# Revit family: GMV-ND22-100TC-T
name_source: partatom
category: 机械设备
revit_build: Autodesk Revit 2014 (Build: 20130308_1515(x64)
units: mm (PartAtom-declared; Revit-internal decimal feet)

## types (11) — shared parameters
Drainage Pipe = 25  [stored 0.082021 ft]
Main Body Height = 280  [stored 0.918635 ft]
Main Body Width = 840  [stored 2.75591 ft]
Main body Depth = 840  [stored 2.75591 ft]
Panel Depth = 950
Panel Height = 65
Panel Width = 950
Power supply = 220-240V 1 phase ~50Hz/208-230V 1 phase ~60Hz
主体 = 锌板
主体宽 = 840  [stored 2.75591 ft]
主体深 = 840  [stored 2.75591 ft]
主体高 = 280  [stored 0.918635 ft]
出风口上边到中心线距离 = 380
出风口下边到中心线距离 = 330
出风口右边到中心线距离 = 200  [stored 0.656168 ft]
出风口宽度 = 50  [stored 0.164042 ft]
出风口左边到中心线距离 = 200  [stored 0.656168 ft]
出风口长度 = 400  [stored 1.31234 ft]
吊装孔直径 = 21.71
吊装孔高 = 80
吊装螺杆间距 = 300
回风口边距中心线距离 = 250
回风口长度和宽度 = 500
气管距中心线距离 = 252
气管距面板上边高度 = 89
液管距中心线距离 = 314
液管距面板上边高度 = 115
面板 = ABS

## per-type parameters (varying)
| type | Gas pipe | Liquid pipe | Net weight Main body/Panel(kg) | Sound Pressure Level (H/M/L)(dB) |
| GMV-ND28T/C-T | 9.52 | 6.35  [stored 0.0208333 ft] | 27/6 | 33/30/28 |
| GMV-ND36T/C-T | 9.52 | 6.35  [stored 0.0208333 ft] | 27/6 | 33/30/28 |
| GMV-ND45T/C-T | 9.52 | 6.35  [stored 0.0208333 ft] | 27/6 | 34/30/28 |
| GMV-ND50T/C-T | 9.52 | 6.35  [stored 0.0208333 ft] | 28/6 | 35/32/29 |
| GMV-ND56T/C-T | 15.9 | 9.52 | 28/6 | 37/33/30 |
| GMV-ND63T/C-T | 15.9 | 9.52 | 35/7 | 37/34/31 |
| GMV-ND71T/C-T | 15.9 | 9.52 | 28/6 | 37/34/31 |
| GMV-ND80T/C-T | 15.9 | 9.52 | 29/6 | 39/37/34 |
| GMV-ND90T/C-T | 15.9 | 9.52 | 29/6 | 39/37/34 |
| GMV-ND100T/C-T | 15.9 | 9.52 | 29/6 | 39/37/34 |
| GMV-ND22T/C-T | 9.52 | 6.35  [stored 0.0208333 ft] | 27/6 | 33/30/28 |

note: [stored X ft] marks values corroborated as IEEE doubles in the binary element streams (Revit-internal decimal feet)
